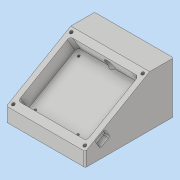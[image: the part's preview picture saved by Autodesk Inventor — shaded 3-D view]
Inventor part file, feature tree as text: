
AUTODESK INVENTOR PART (.ipt)
format: ipt  version: 2018 (Build 220112000, 112)  size: 207,360 bytes
history: native  units: mm
features: sketch x8, reference x8, extrude x4, hole x4, other x4, fillet x3, projected_geometry x1
ambient origin geometry x8: Origin, YZ Plane, XZ Plane, XY Plane, X Axis, Y Axis, Z Axis, Center Point
bodies: Volumenkörper1 (feature_tree)
feature tree (32):
  extrude  "Extrusion1"  Depth=95.0mm
  extrude  "Extrusion2"  Depth=15.0mm
  extrude  "Extrusion3"  TaperAngle=120.0deg  [1 undecoded]
  extrude  "Extrusion4"  Depth=74.0mm
  fillet  "Rundung2"  Radius=64.5mm
  hole  "Bohrung2"  [1 undecoded]
  hole  "Bohrung3"  [1 undecoded]
  hole  "Bohrung4"  [1 undecoded]
  hole  "Bohrung5"  [1 undecoded]
  fillet  "Rundung3"  Radius=20.0mm
  fillet  "Rundung1"  Radius=1.5mm
  sketch  "Skizze1"  dims[d0=85.0mm d1=95.0mm]
  sketch  "Skizze2"  dims[d2=80.0mm d3=0.0mm d4=15.0mm]
  sketch  "Skizze3"  dims[d5=80.0mm d6=120.0deg]
  sketch  "Skizze4"  dims[d7=80.0mm d8=0.0mm d9=74.0mm d10=64.5mm]
  sketch  "Skizze6"  dims[d11=16.36mm d12=0.0mm d13=8.0mm]
  reference  "Referenz5"
  reference  "Referenz6"
  reference  "Referenz7"
  reference  "Referenz8"
  sketch  "Skizze7"  dims[d14=3.1mm d15=4.1mm]
  projected_geometry  "Projizierte Kontur1"
  sketch  "Skizze8"  dims[d16=3.15mm d17=12.2mm]
  reference  "Referenz9"
  reference  "Referenz11"
  reference  "Referenz12"
  reference  "Referenz13"
  sketch  "Skizze9"  dims[d18=10.8mm d19=1.46mm d20=20.0mm d21=0.0mm d22=1.5mm d30=3.242mm d31=8.0mm d32=4.0mm d33=2.0mm d34=90.0deg d35=11.8mm d36=20.594885mm d37=42.5mm d38=14.0mm d39=10.0mm d40=8.0mm d41=4.0mm d42=2.0mm d43=90.0deg d44=11.8mm d45=20.594885mm d46=1.5mm d47=2.459mm d48=6.0mm d49=4.0mm d50=2.0mm d51=90.0deg d52=7.0mm d53=20.594885mm d54=60.0mm d55=41.0mm d56=7.0mm d57=7.0mm d58=4.917mm d59=16.0mm d60=4.0mm d61=2.0mm d62=90.0deg d63=20.0mm d64=20.594885mm]
  other  "<userpath>\Documents\Waage\CAD\Main.iam"
  other  "Main.iam"
  other  "Schiled:1"
  other  "WaagePCB:1"
note: 5 required parameter values undecoded (feature->parameter linkage not recoverable at this tier; creation-order binding heuristic only, values carry confidence <= 0.55)
